# Revit family: Haworth_Massimosistema_PeninsularModule_OneArm
name_source: partatom
category: Furniture
revit_build: Autodesk Revit 2018 (Build: 20170223_1515(x64)
units: mm (PartAtom-declared; Revit-internal decimal feet)

## family parameters
Always vertical = Yes
Cut with Voids When Loaded = No
OmniClass Number = 23.40.20.00
OmniClass Title = General Furniture and Specialties
Room Calculation Point = No
Shared = No
Work Plane-Based = No

## types (2) — shared parameters
Actual Depth = 55"
Actual Height = 33 3/4"
Assembly Code = E2020200
Cushion Width = 48 3/4"
Frame Finish = Haworth _ Paint _ Metallic Gunmetal
Manufacturer = Haworth
Model = HCPF-MSPX
Seat Depth = 34 3/4"
Size = Verify Final Dim. w/ Haworth
URL = http://www.haworth.com
URL - Product = http://www.haworth.com
Version = 1
Warranty = https://www.haworth.com

## per-type parameters (varying)
| type | Actual Width | Arm Height | Arm Width | Back End | Description | High | Low |
| HCPF-MSPX-H0 | 55" | 28" | 6 1/4" | 55" | Haworth Massimosistema Sofa - Peninsular Module - High One Arm | Yes | No |
| HCPF-MSPX-L0 | 56 3/4" | 22 3/4" | 8" | 56 3/4" | Haworth Massimosistema Sofa - Peninsular Module - Low One Arm | No | Yes |

## geometry (parser evidence)
native form markers: Sweep x8
no freeform markers — native parametric forms only
